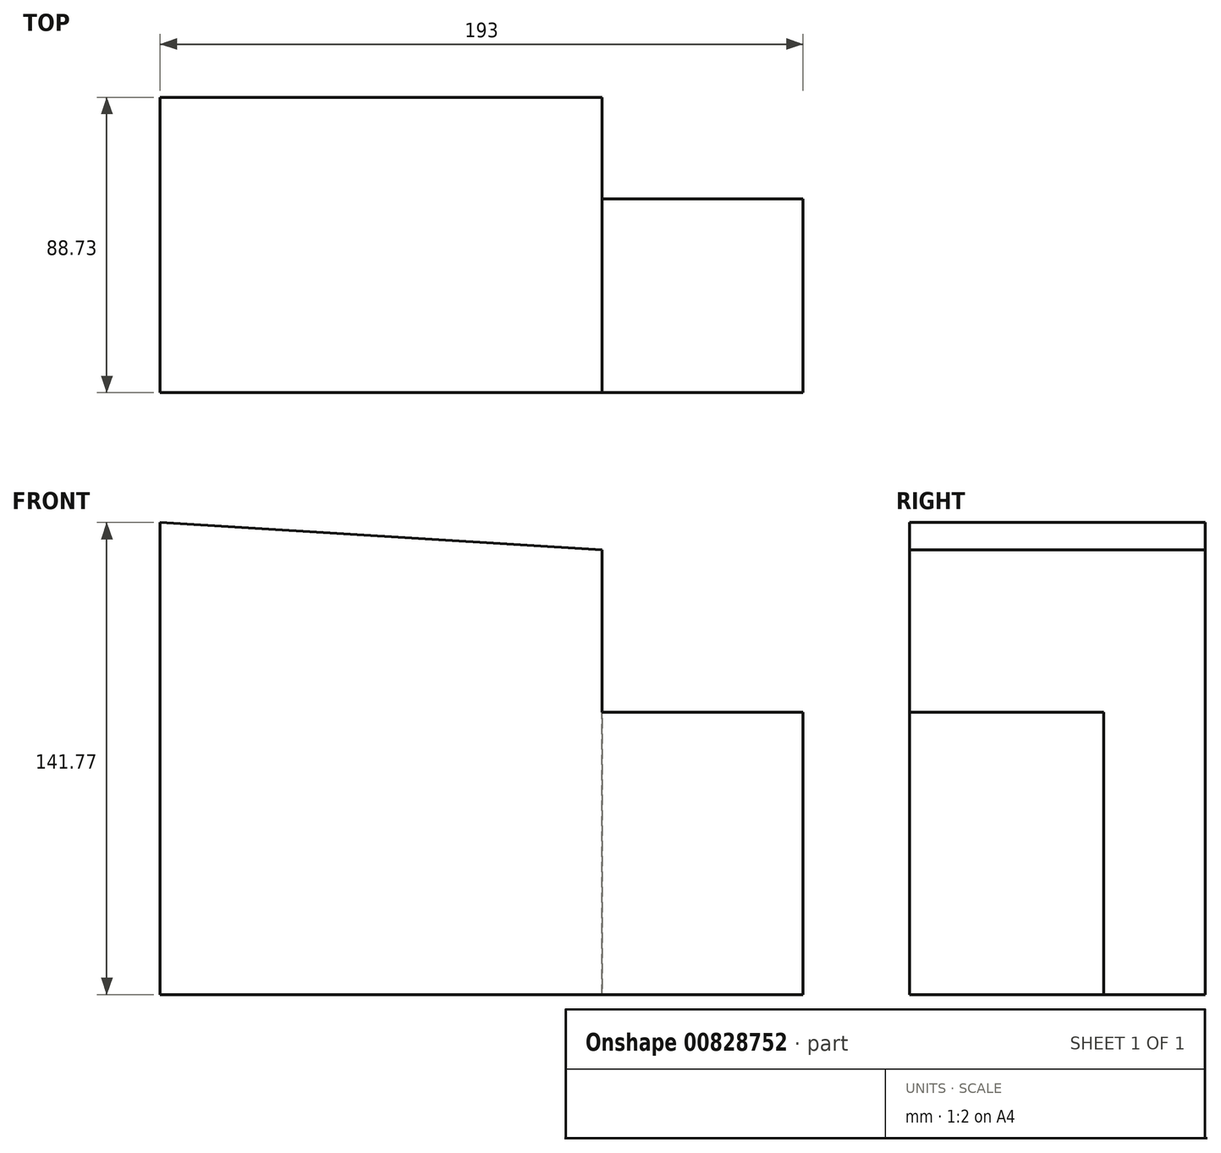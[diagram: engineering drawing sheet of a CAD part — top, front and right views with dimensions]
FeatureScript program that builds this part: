
annotation { "Feature Type Name" : "Feature", "Feature Type Description" : "" }
export const myFeature = defineFeature(function(context is Context, id is Id, definition is map)
    precondition{}
    {
        {
            var Q0;
            Q0=qCreatedBy(makeId("Front.planeOp"),FACE);
            var sketch = newSketch(context, id + "F0", { "sketchPlane" : qUnion([Q0])});
            skLineSegment(sketch, "E0", {"start": v(42.22, 96.17) * mm, "end": v(42.22, 96.17) * mm});
            skLineSegment(sketch, "E1", {"start": v(42.22, 96.17) * mm, "end": v(42.22, -37.4) * mm});
            skLineSegment(sketch, "E2", {"start": v(42.22, -37.4) * mm, "end": v(-90.42, -37.4) * mm});
            skLineSegment(sketch, "E3", {"start": v(-90.42, -37.4) * mm, "end": v(-90.42, 104.38) * mm});
            skLineSegment(sketch, "E4", {"start": v(-90.42, 104.38) * mm, "end": v(42.22, 96.17) * mm});
            skLineSegment(sketch, "E5", {"start": v(-90.42, 104.38) * mm, "end": v(-90.42, 87.38) * mm});
            skSolve(sketch);
        }
        {
            var Q0;
            Q0 = qSketchRegion(id + "F0", true);
            extrude(context, id + "F1", {"entities" : qUnion([Q0]), "depth" : 88.73 * mm, "offsetDistance" : 25.4 * mm});
        }
        {
            var Q0;
            Q0=makeQuery(id+"F1.opExtrude","SWEPT_FACE",FACE,{"disambiguationData":[OSD([sQuery(id+"F0.wireOp",EDGE,"E2")])]});
            var sketch = newSketch(context, id + "F2", { "sketchPlane" : qUnion([Q0])});
            skLineSegment(sketch, "E6.bottom", {"start": v(-54.2, 30.5) * mm, "end": v(102.58, 30.5) * mm});
            skLineSegment(sketch, "E6.top", {"start": v(-54.2, 88.73) * mm, "end": v(102.58, 88.73) * mm});
            skLineSegment(sketch, "E6.left", {"start": v(-54.2, 30.5) * mm, "end": v(-54.2, 88.73) * mm});
            skLineSegment(sketch, "E6.right", {"start": v(102.58, 30.5) * mm, "end": v(102.58, 88.73) * mm});
            skSolve(sketch);
        }
        {
            var Q0;
            Q0 = qSketchRegion(id + "F2", true);
            extrude(context, id + "F3", {"entities" : qUnion([Q0]), "operationType" : NewBodyOperationType.ADD, "oppositeDirection" : true, "depth" : 84.74 * mm, "offsetDistance" : 25.4 * mm});
        }
    });
